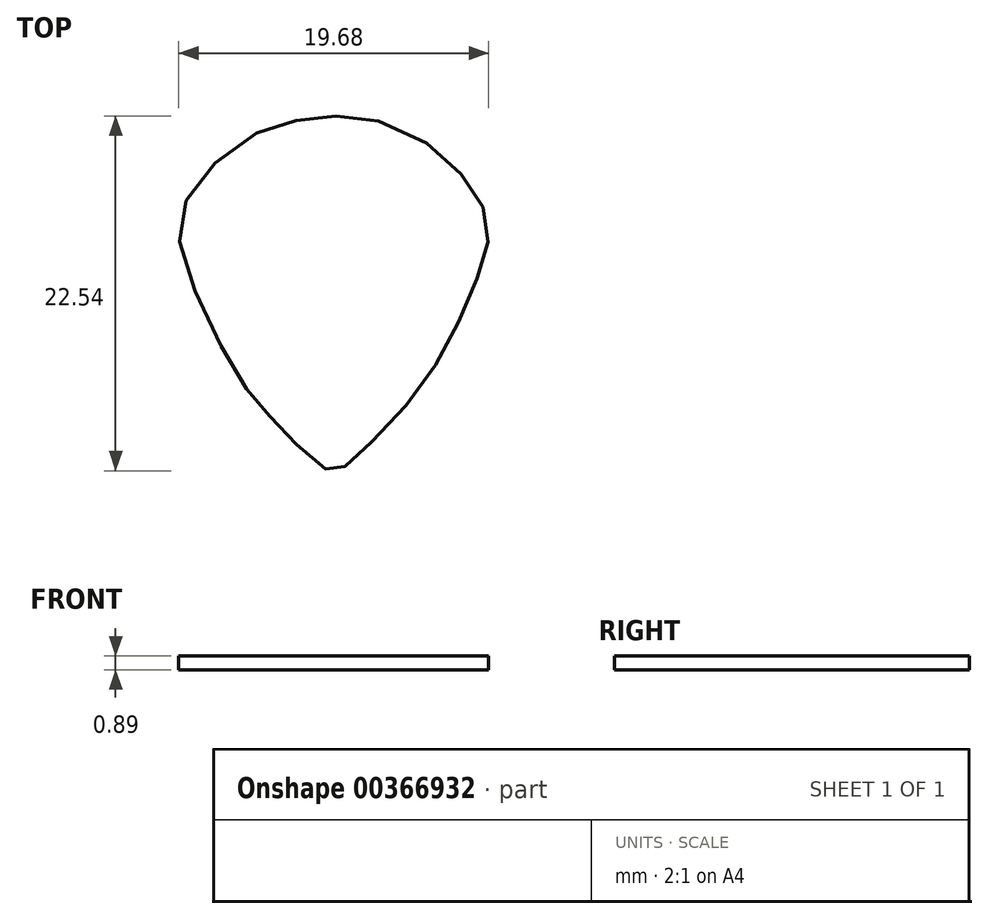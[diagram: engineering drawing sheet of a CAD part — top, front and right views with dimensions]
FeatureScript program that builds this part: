
annotation { "Feature Type Name" : "Feature", "Feature Type Description" : "" }
export const myFeature = defineFeature(function(context is Context, id is Id, definition is map)
    precondition{}
    {
        {
            var Q0;
            Q0=qCreatedBy(makeId("Top.planeOp"),FACE);
            var sketch = newSketch(context, id + "F0", { "sketchPlane" : qUnion([Q0])});
            skPoint(sketch, "E0.12.internal.snap0", {"position": v(-7.29, -6.46) * mm});
            skFitSpline(sketch, "E0", {"points": [v(-7.25, 18.54) * mm, v(-4.6, 18.23) * mm, v(-0.98, 16.49) * mm, v(1.06, 14.4) * mm, v(2.19, 12.53) * mm, v(2.45, 10.74) * mm, v(1.97, 8.87) * mm, v(0.8, 5.98) * mm, v(-0.8, 2.95) * mm, v(-2.92, 0) * mm, v(-5.37, -2.56) * mm, v(-6.61, -3.69) * mm, v(-7.29, -3.98) * mm, v(-7.8, -3.92) * mm, v(-9.27, -2.8) * mm, v(-10.85, -1.17) * mm, v(-12.16, 0.26) * mm, v(-13.5, 2.08) * mm, v(-15.76, 6.5) * mm, v(-17.17, 10.45) * mm, v(-16.86, 12.95) * mm, v(-14.92, 15.54) * mm, v(-11.87, 17.64) * mm, v(-9.58, 18.29) * mm, v(-7.25, 18.54) * mm]});
            skSolve(sketch);
        }
        {
            var Q0;
            Q0 = qSketchRegion(id + "F0", true);
            extrude(context, id + "F1", {"entities" : qUnion([Q0]), "depth" : 0.89 * mm});
        }
    });
